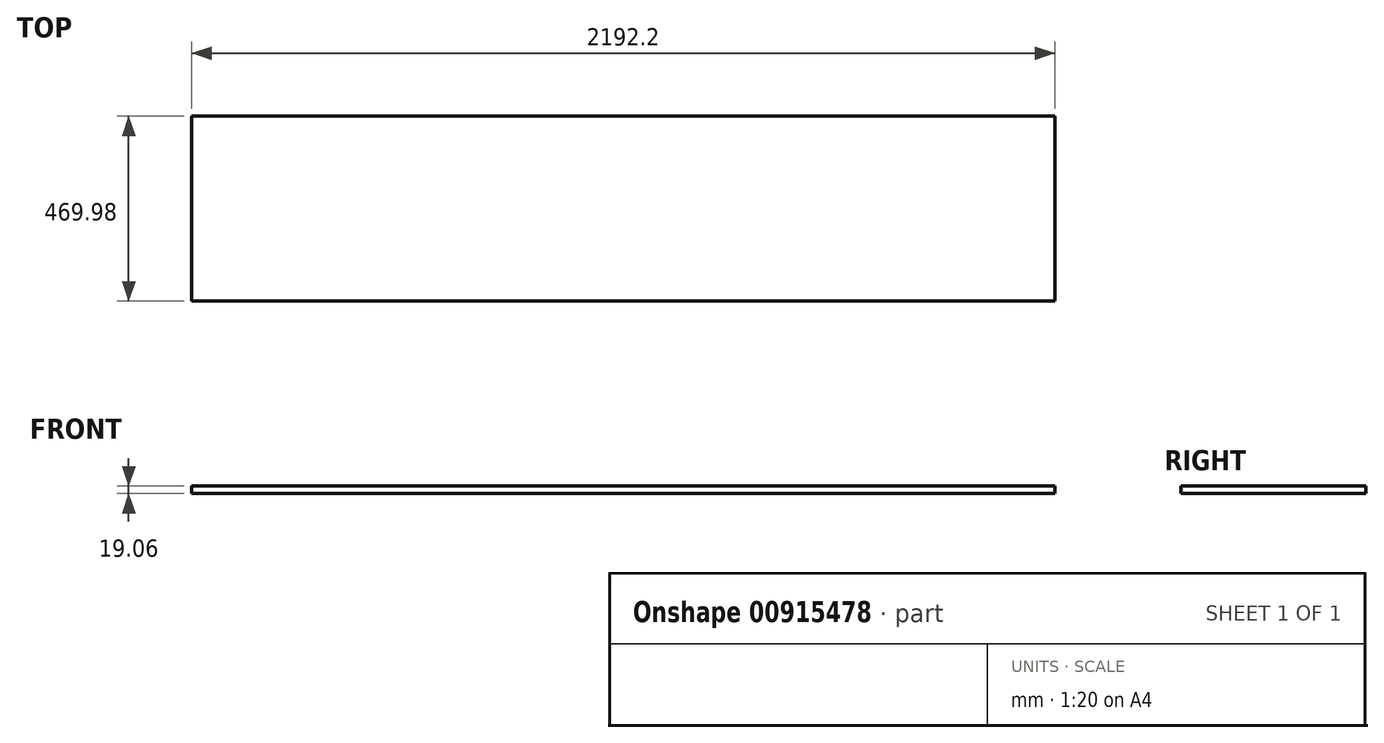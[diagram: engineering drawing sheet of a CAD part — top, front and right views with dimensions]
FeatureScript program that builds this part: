
annotation { "Feature Type Name" : "Feature", "Feature Type Description" : "" }
export const myFeature = defineFeature(function(context is Context, id is Id, definition is map)
    precondition{}
    {
        {
            var Q0;
            Q0=qCreatedBy(makeId("Right.planeOp"),FACE);
            var sketch = newSketch(context, id + "F0", { "sketchPlane" : qUnion([Q0])});
            skLineSegment(sketch, "E0.bottom", {"start": v(234.99, 9.53) * mm, "end": v(-234.99, 9.53) * mm});
            skLineSegment(sketch, "E0.top", {"start": v(234.99, -9.53) * mm, "end": v(-234.99, -9.53) * mm});
            skLineSegment(sketch, "E0.left", {"start": v(234.99, 9.53) * mm, "end": v(234.99, -9.53) * mm});
            skLineSegment(sketch, "E0.right", {"start": v(-234.99, 9.53) * mm, "end": v(-234.99, -9.53) * mm});
            skPoint(sketch, "E0.middle", {"position": v(0, 0) * mm});
            skSolve(sketch);
        }
        {
            var Q0;
            Q0=makeQuery(id+"F0.imprint","IMPRINT",FACE,{"disambiguationData":[TD([[makeQuery(id+"F0.imprint","IMPRINT",EDGE,{"derivedFrom":sQuery(id+"F0.wireOp",EDGE,"E0.bottom")}),1.0]])]});
            extrude(context, id + "F1", {"entities" : qUnion([Q0]), "depth" : 2192.2 * mm, "offsetDistance" : 25.4 * mm});
        }
    });
